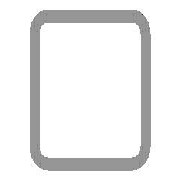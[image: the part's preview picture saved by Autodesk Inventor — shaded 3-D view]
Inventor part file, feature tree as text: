
AUTODESK INVENTOR PART (.ipt)
format: ipt  version: 2025 (Build 290162010, 162A)  size: 133,120 bytes
history: native  units: mm (DEFAULTED — no unit token found)
features: other x4, sketch x1, plane x1
ambient origin geometry x8: Origin, YZ Plane, XZ Plane, XY Plane, X Axis, Y Axis, Z Axis, Center Point
bodies: Solid1 (feature_tree), Body (feature_tree)
feature tree (6):
  parser-record x1  (decoder bookkeeping rows leaked as tree rows — omitted from the tree; the rows remain in map.json)
  other  "Driven Length"
  other  "Start Plane"
  other  "End Plane"
  sketch  "Sketch3"  dims[d3=710.0mm d4=0.0mm d7=4.0mm d9=40.0mm d11=40.0mm d12=2.0mm d13=-0.0mm d14=710.0mm d15=20.0mm d16=20.0mm d17=90.0deg d18=710.0mm]
  plane  "Work Plane3"
